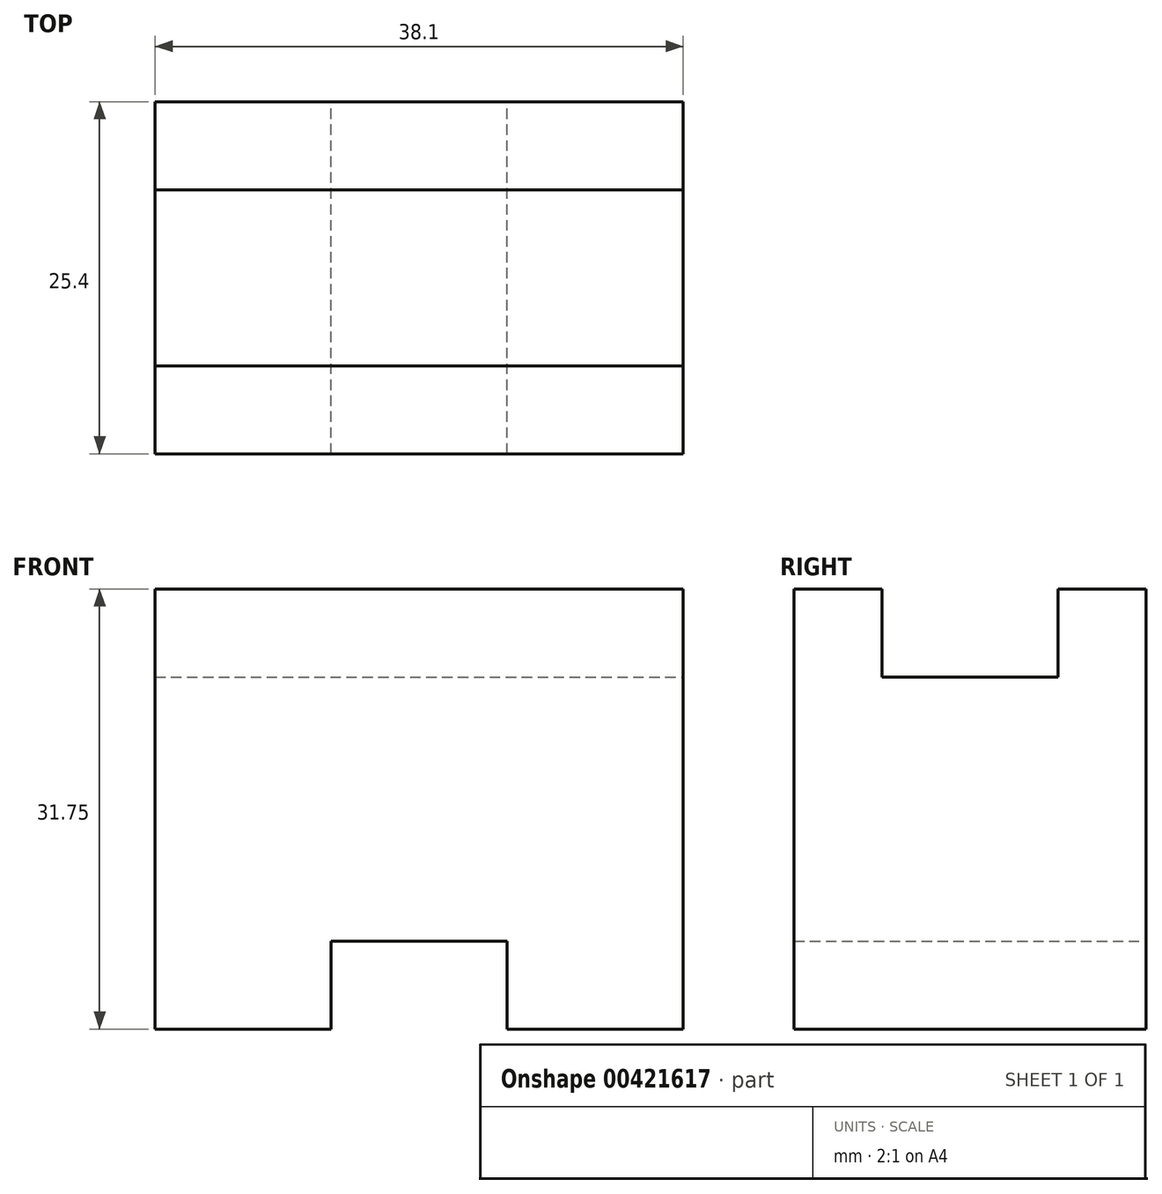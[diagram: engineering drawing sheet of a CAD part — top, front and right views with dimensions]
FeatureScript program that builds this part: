
annotation { "Feature Type Name" : "Feature", "Feature Type Description" : "" }
export const myFeature = defineFeature(function(context is Context, id is Id, definition is map)
    precondition{}
    {
        {
            var Q0;
            Q0=qCreatedBy(makeId("Front.planeOp"),FACE);
            var sketch = newSketch(context, id + "F0", { "sketchPlane" : qUnion([Q0])});
            skLineSegment(sketch, "E0", {"start": v(0, 0) * mm, "end": v(0, 31.75) * mm});
            skLineSegment(sketch, "E1", {"start": v(0, 31.75) * mm, "end": v(38.1, 31.75) * mm});
            skLineSegment(sketch, "E2", {"start": v(38.1, 31.75) * mm, "end": v(38.1, 0) * mm});
            skLineSegment(sketch, "E3", {"start": v(0, 0) * mm, "end": v(12.7, 0) * mm});
            skLineSegment(sketch, "E4", {"start": v(12.7, 0) * mm, "end": v(12.7, 6.35) * mm});
            skLineSegment(sketch, "E5", {"start": v(12.7, 6.35) * mm, "end": v(25.4, 6.35) * mm});
            skLineSegment(sketch, "E6", {"start": v(25.4, 6.35) * mm, "end": v(25.4, 0) * mm});
            skLineSegment(sketch, "E7", {"start": v(25.4, 0) * mm, "end": v(38.1, 0) * mm});
            skSolve(sketch);
        }
        {
            var Q0;
            Q0=makeQuery(id+"F0.imprint","IMPRINT",FACE,{"disambiguationData":[TD([[makeQuery(id+"F0.imprint","IMPRINT",EDGE,{"derivedFrom":sQuery(id+"F0.wireOp",EDGE,"E0")}),-1.0]])]});
            extrude(context, id + "F1", {"entities" : qUnion([Q0]), "depth" : 25.4 * mm});
        }
        {
            var Q0;
            Q0=makeQuery(id+"F1.opExtrude","SWEPT_FACE",FACE,{"disambiguationData":[OSD([sQuery(id+"F0.wireOp",EDGE,"E2")])]});
            var sketch = newSketch(context, id + "F2", { "sketchPlane" : qUnion([Q0])});
            skLineSegment(sketch, "E8", {"start": v(-25.4, 31.75) * mm, "end": v(-19.05, 31.75) * mm});
            skLineSegment(sketch, "E9", {"start": v(-19.05, 31.75) * mm, "end": v(-19.05, 25.4) * mm});
            skLineSegment(sketch, "E10", {"start": v(-19.05, 25.4) * mm, "end": v(-6.35, 25.4) * mm});
            skLineSegment(sketch, "E11", {"start": v(-6.35, 25.4) * mm, "end": v(-6.35, 31.75) * mm});
            skSolve(sketch);
        }
        {
            var Q0;
            {var subQ0=sQuery(id+"F2.wireOp",EDGE,"E9");Q0=makeQuery(id+"F2.imprint","IMPRINT",FACE,{"disambiguationData":[TD([[makeQuery(id+"F2.imprint","IMPRINT",EDGE,{"derivedFrom":subQ0}),1.0]])]});}
            extrude(context, id + "F3", {"entities" : qUnion([Q0]), "operationType" : NewBodyOperationType.REMOVE, "oppositeDirection" : true, "depth" : 38.1 * mm});
        }
    });
